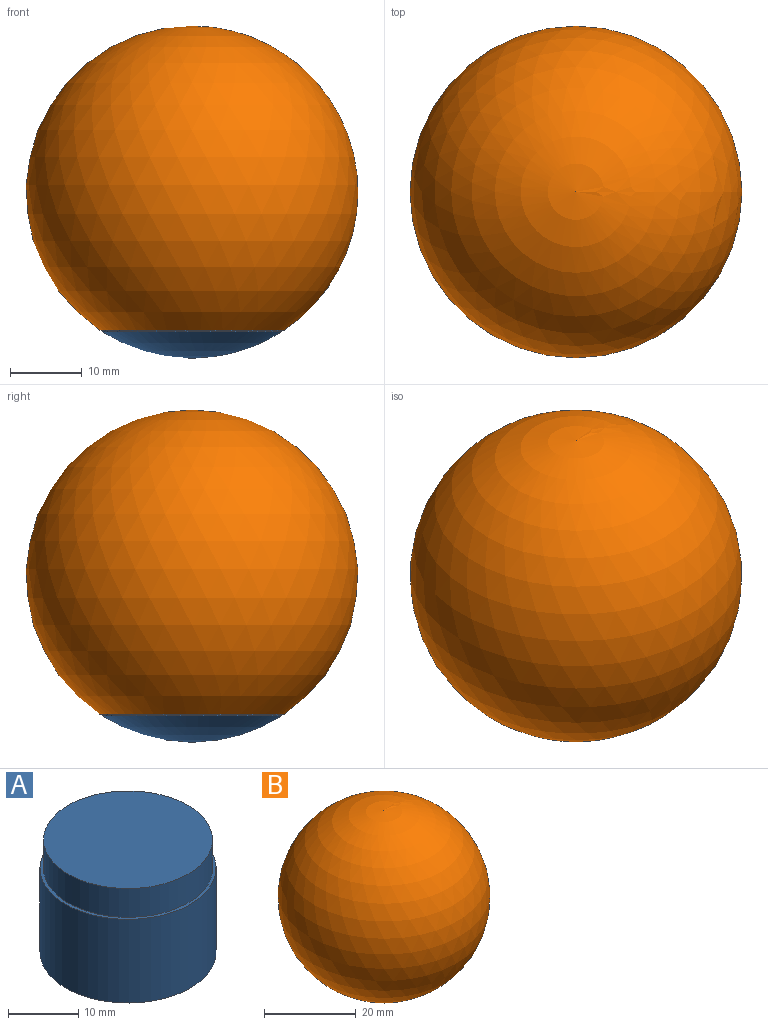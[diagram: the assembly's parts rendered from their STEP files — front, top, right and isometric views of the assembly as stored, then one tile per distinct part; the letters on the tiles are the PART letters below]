
ASSEMBLY  parts=2 mates=1
PART A: 7 faces, bbox 25x25x23.2 mm
  f0: cylinder r=0.5mm len=2mm, axis (0,0,1), area 6.3mm2, adj f1,f6
  f1: sphere r=23.2mm, area 532.1mm2, adj f0,f2
  f2: cylinder r=12.5mm len=25mm, axis (0,0,1), area 1142.3mm2, adj f1,f3
  f3: plane 25x25mm, normal (0,0,1), area 38.5mm2, adj f2,f4
  f4: cylinder r=12mm len=24mm, axis (0,0,1), area 377mm2, adj f3,f5
  f5: plane 24x24mm, normal (0,0,1), area 452.4mm2, adj f4
  f6: plane 1x1mm, normal (0,0,-1), area 0.8mm2, adj f0
PART B: 5 faces, bbox 46.4x46.4x42.5 mm
  f0: cylinder r=12.9mm len=25.8mm, axis (0,0,1), area 1157.7mm2, adj f1,f4
  f1: sphere r=23.2mm, area 6192.7mm2, adj f0
  f2: sphere r=12.4mm, area 966.1mm2, adj f3
  f3: cylinder r=12.4mm len=24.8mm, axis (0,0,1), area 389.6mm2, adj f2,f4
  f4: plane 25.8x25.8mm, normal (0,0,-1), area 39.7mm2, adj f0,f3
PLACE A t=(-12.64,-10.56,-1.54)mm
PLACE B t=(-12.64,-10.56,19.81)mm
MATE fastened B.f0 <-> A.f0  axis (0,0,-1) through (-12.64,-10.56,14.81)mm
